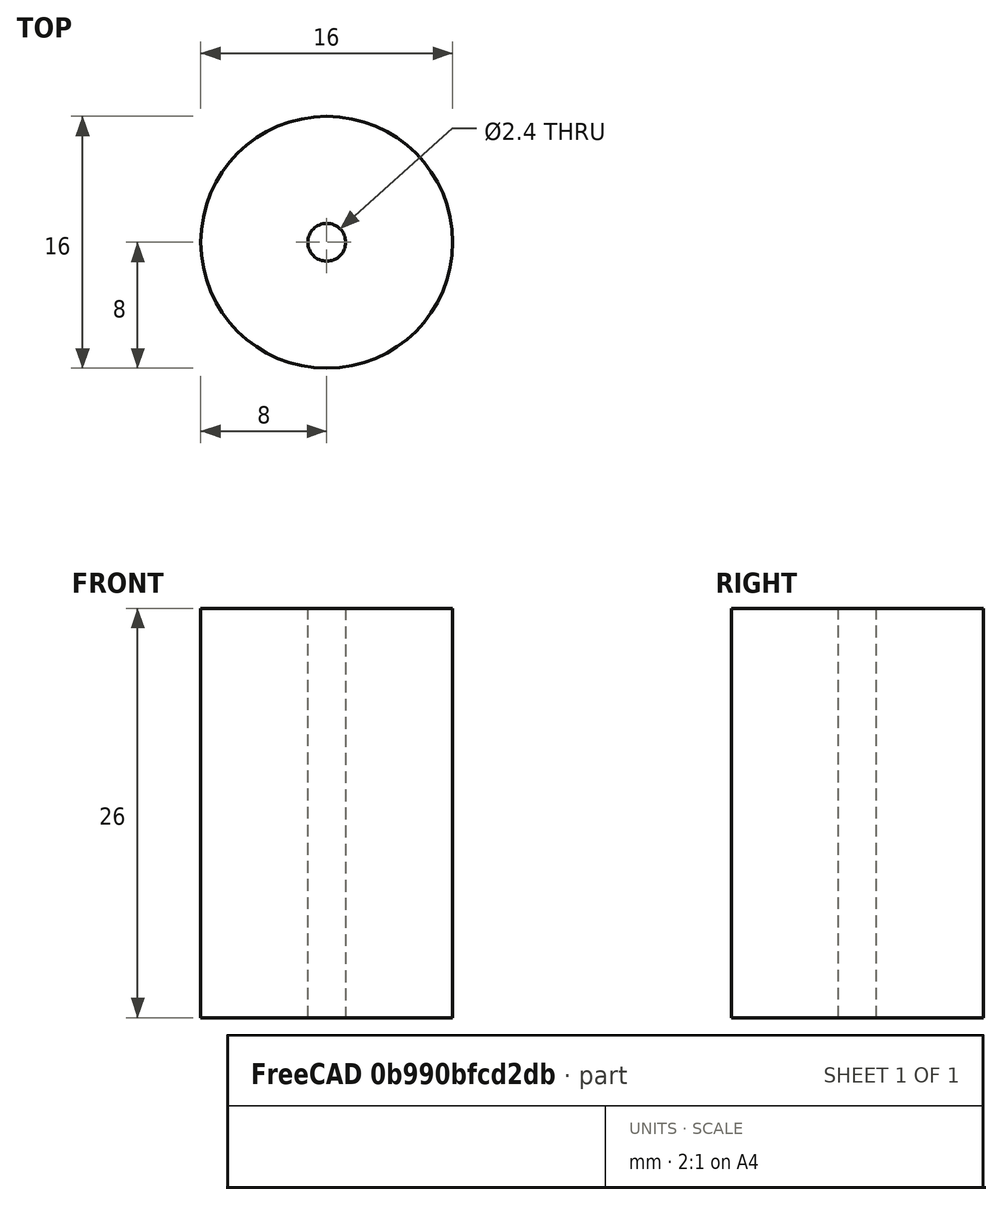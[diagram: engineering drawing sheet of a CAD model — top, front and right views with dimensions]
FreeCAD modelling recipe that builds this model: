
FCSTD DOCUMENT  (FreeCAD 0.21R33668 +26 (Git))
Label: board_connector_top_mid
License: All rights reserved
LicenseURL: https://en.wikipedia.org/wiki/All_rights_reserved
objects: Sketcher::SketchObject×2, PartDesign::Pad×1, PartDesign::Pocket×1, PartDesign::Body×1
note: 7 computed .brp shape members not serialized (recipe doc carries the construction recipe); baked Part::Feature solids carry a one-line shape summary decoded from their .brp

FEATURE [Sketcher::SketchObject] Sketch
  FullyConstrained = false
  MapMode = 5
  Support = -> [XY_Plane]
  sketch-geometry (2):
    g0: Circle CenterX=0 CenterY=0 CenterZ=0 NormalX=0 NormalY=0 NormalZ=1 AngleXU=0 Radius=8
    g1: GeomPoint X=-5.04833 Y=6.206 Z=0
  constraints (3):
    c: Coincident(g0,g-1)
    c: PointOnObject(g1,g0)
    c: Distance(g1,g0) = 8
FEATURE [PartDesign::Pad] Pad
  Direction = (0,0,1)
  Length = 26
  Length2 = 10
  Profile = -> Sketch
  ReferenceAxis = -> Sketch [N_Axis]
  Type = 0
FEATURE [Sketcher::SketchObject] Sketch001
  FullyConstrained = false
  MapMode = 5
  Placement = pos=(0,0,26) rot=(0,0,1;0rad)
  Support = -> [Pad]
  sketch-geometry (2):
    g0: Circle CenterX=0 CenterY=0 CenterZ=0 NormalX=0 NormalY=0 NormalZ=1 AngleXU=0 Radius=1.2
    g1: GeomPoint X=-0.940143 Y=0.745742 Z=0
  constraints (3):
    c: Coincident(g0,g-1)
    c: PointOnObject(g1,g0)
    c: Distance(g1,g0) = 1.2
FEATURE [PartDesign::Pocket] Pocket
  BaseFeature = -> Pad
  Direction = (0,0,-1)
  Length = 35
  Length2 = 5
  Profile = -> Sketch001
  ReferenceAxis = -> Sketch001 [N_Axis]
  Type = 0
FEATURE [PartDesign::Body] Body
  Group = -> [Sketch,Pad,Sketch001,Pocket]
  Origin = -> Origin
  Tip = -> Pocket
